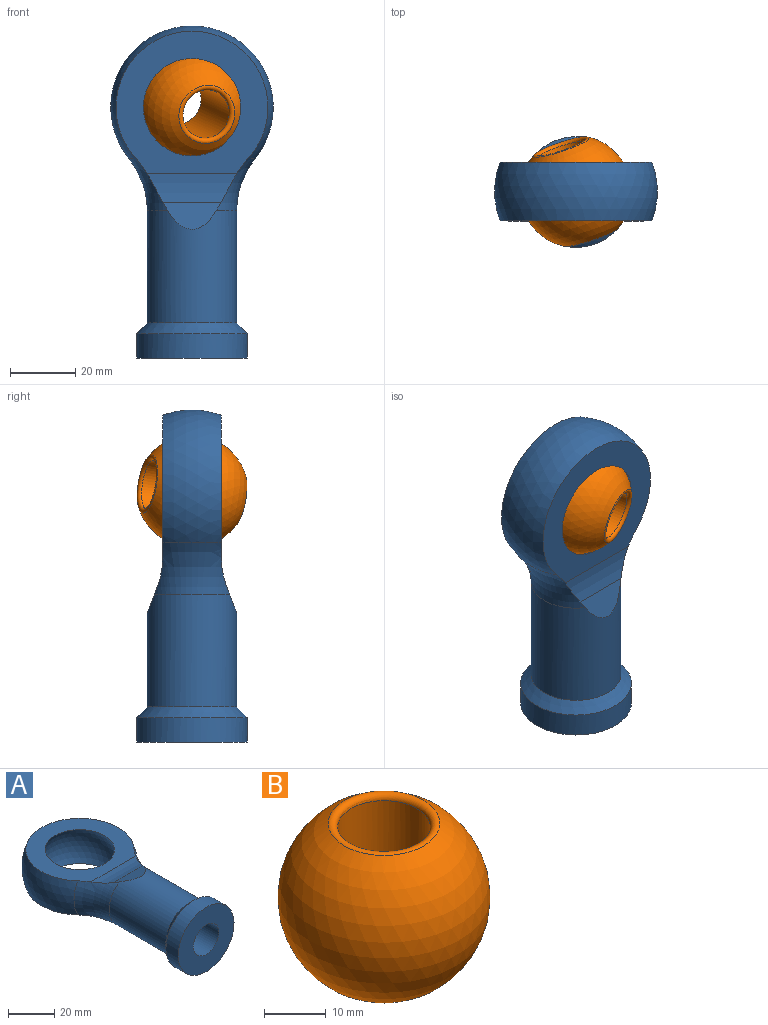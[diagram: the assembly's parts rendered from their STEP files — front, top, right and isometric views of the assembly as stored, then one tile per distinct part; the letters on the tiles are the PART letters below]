
ASSEMBLY  parts=2 mates=1
PART A: 16 faces, bbox 50x102x38.1 mm
  f0: cylinder r=13.75mm len=34.65mm, axis (0,1,0), area 2869.1mm2, adj f3,f4,f7,f10,f15
  f1: sphere r=25mm, area 2046.5mm2, adj f2,f5,f7,f10
  f2: plane 46.68x43.76mm, normal (0,0,-1), area 968.1mm2, adj f1,f6,f7,f8,f10
  f3: plane 17.78x8.21mm, normal (0,0.36,-0.93), area 105mm2, adj f0,f7,f8,f10
  f4: plane 17.78x8.21mm, normal (0,0.36,0.93), area 105mm2, adj f0,f7,f9,f10
  f5: plane 46.68x43.76mm, normal (0,0,1), area 968.1mm2, adj f1,f6,f7,f9,f10
  f6: sphere r=17.46mm, area 1975mm2, adj f2,f5
  f7: torus R=38.75mm, axis (0,1,0), area 356.3mm2, adj f0,f1,f2,f3,f4,f5,f8,f9
  f8: cylinder r=25mm len=27.4mm, axis (1,0,0), area 204.4mm2, adj f2,f3,f7,f10
  f9: cylinder r=25mm len=27.4mm, axis (1,0,0), area 204.4mm2, adj f4,f5,f7,f10
  f10: torus R=38.75mm, axis (0,1,0), area 356.3mm2, adj f0,f1,f2,f3,f4,f5,f8,f9
  f11: cylinder r=17mm len=34mm, axis (0,-1,0), area 801.1mm2, adj f12,f15
  f12: plane 34x34mm, normal (0,-1,0), area 719.2mm2, adj f11,f13
  f13: cylinder r=7.75mm len=29.75mm, axis (0,-1,0), area 1448.7mm2, adj f12,f14
  f14: cone r=7.75mm half-angle=45deg, axis (0,-1,0), area 266.9mm2, adj f13
  f15: cone r=13.75mm half-angle=45deg, axis (0,-1,0), area 444mm2, adj f0,f11
PART B: 4 faces, bbox 34.3x34.3x29.5 mm
  f0: sphere r=17.16mm, area 3148.2mm2, adj f2,f3
  f1: cylinder r=7.5mm len=27.49mm, axis (0,0,-1), area 1295.6mm2, adj f2,f3
  f2: torus R=8.5mm, axis (0,0,1), area 108.1mm2, adj f0,f1
  f3: torus R=8.5mm, axis (0,0,-1), area 108.1mm2, adj f0,f1
PLACE A rot(axis=(1,0,0),90deg) t=(0,0,77)mm
PLACE B rot(axis=(0.97,0.02,0.24),102.9deg) t=(0,0,77)mm
MATE ball B.f1 <-> A.f6  axis (0.31,-0.94,-0.15) through (0,0,77)mm
